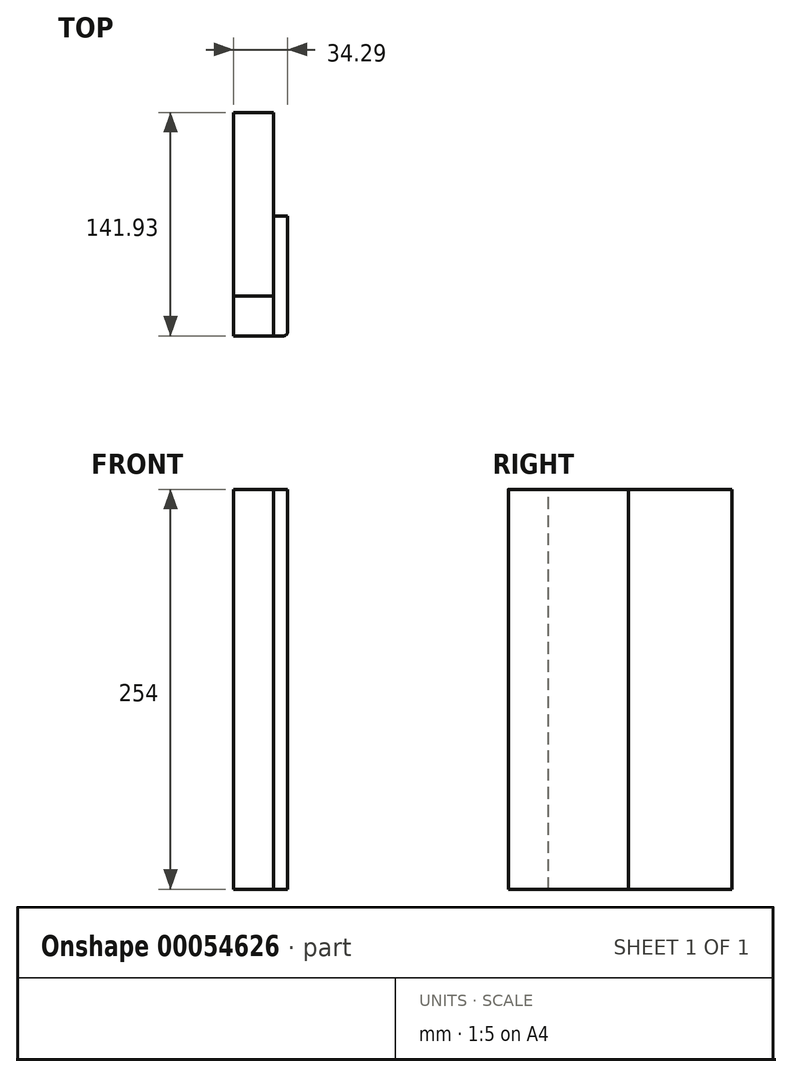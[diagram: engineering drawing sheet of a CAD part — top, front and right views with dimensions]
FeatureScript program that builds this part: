
annotation { "Feature Type Name" : "Feature", "Feature Type Description" : "" }
export const myFeature = defineFeature(function(context is Context, id is Id, definition is map)
    precondition{}
    {
        {
            var Q0;
            Q0=qCreatedBy(makeId("Right.planeOp"),FACE);
            var sketch = newSketch(context, id + "F0", { "sketchPlane" : qUnion([Q0])});
            skLineSegment(sketch, "E0.bottom", {"start": v(0, 0) * mm, "end": v(116.53, 0) * mm});
            skLineSegment(sketch, "E0.top", {"start": v(0, 254) * mm, "end": v(116.53, 254) * mm});
            skLineSegment(sketch, "E0.left", {"start": v(0, 0) * mm, "end": v(0, 254) * mm});
            skLineSegment(sketch, "E0.right", {"start": v(116.53, 0) * mm, "end": v(116.53, 254) * mm});
            skSolve(sketch);
        }
        {
            var Q0;
            Q0=makeQuery(id+"F0.imprint","IMPRINT",FACE,{"disambiguationData":[TD([[makeQuery(id+"F0.imprint","IMPRINT",EDGE,{"derivedFrom":sQuery(id+"F0.wireOp",EDGE,"E0.bottom")}),1.0]])]});
            extrude(context, id + "F1", {"entities" : qUnion([Q0]), "depth" : 25.4 * mm});
        }
        {
            var Q0;
            Q0=makeQuery(id+"F1.opExtrude","SWEPT_FACE",FACE,{"disambiguationData":[OSD([sQuery(id+"F0.wireOp",EDGE,"E0.left")])]});
            extrude(context, id + "F2", {"entities" : qUnion([Q0]), "depth" : 25.4 * mm});
        }
        {
            var Q0;
            {var subQ0=sQuery(id+"F0.wireOp",EDGE,"E0.left");Q0=makeQuery(id+"F2.opExtrude","SWEPT_FACE",FACE,{"disambiguationData":[OSD([subQ0]),TDD([makeQuery(id+"F1.opExtrude","CAP_EDGE",EDGE,{"disambiguationData":[OSD([subQ0])],"isStart":false})])]});}
            var sketch = newSketch(context, id + "F3", { "sketchPlane" : qUnion([Q0])});
            skLineSegment(sketch, "E1.bottom", {"start": v(-25.4, 254) * mm, "end": v(50.8, 254) * mm});
            skLineSegment(sketch, "E1.top", {"start": v(-25.4, 0) * mm, "end": v(50.8, 0) * mm});
            skLineSegment(sketch, "E1.left", {"start": v(-25.4, 254) * mm, "end": v(-25.4, 0) * mm});
            skLineSegment(sketch, "E1.right", {"start": v(50.8, 254) * mm, "end": v(50.8, 0) * mm});
            skSolve(sketch);
        }
        {
            var Q0;
            {var subQ3=sQuery(id+"F3.wireOp",EDGE,"E1.right");Q0=makeQuery(id+"F3.imprint","IMPRINT",FACE,{"disambiguationData":[TD([[makeQuery(id+"F3.imprint","IMPRINT",EDGE,{"derivedFrom":subQ3}),-1.0]])]});}
            var Q1;
            {var subQ3=sQuery(id+"F3.wireOp",EDGE,"E1.left");Q1=makeQuery(id+"F3.imprint","IMPRINT",FACE,{"disambiguationData":[TD([[makeQuery(id+"F3.imprint","IMPRINT",EDGE,{"derivedFrom":subQ3}),-1.0]])]});}
            extrude(context, id + "F4", {"entities" : qUnion([Q0, Q1]), "depth" : 8.9 * mm});
        }
        {
            var Q0;
            Q0=makeQuery(id+"F4.opExtrude","CAP_EDGE",EDGE,{"disambiguationData":[OSD([sQuery(id+"F3.wireOp",EDGE,"E1.left")])],"isStart":false});
            fillet(context, id + "F5", {"entities" : qUnion([Q0]), "radius" : 2.54 * mm, "tangentPropagation" : true, "allowEdgeOverflow" : false});
        }
    });
